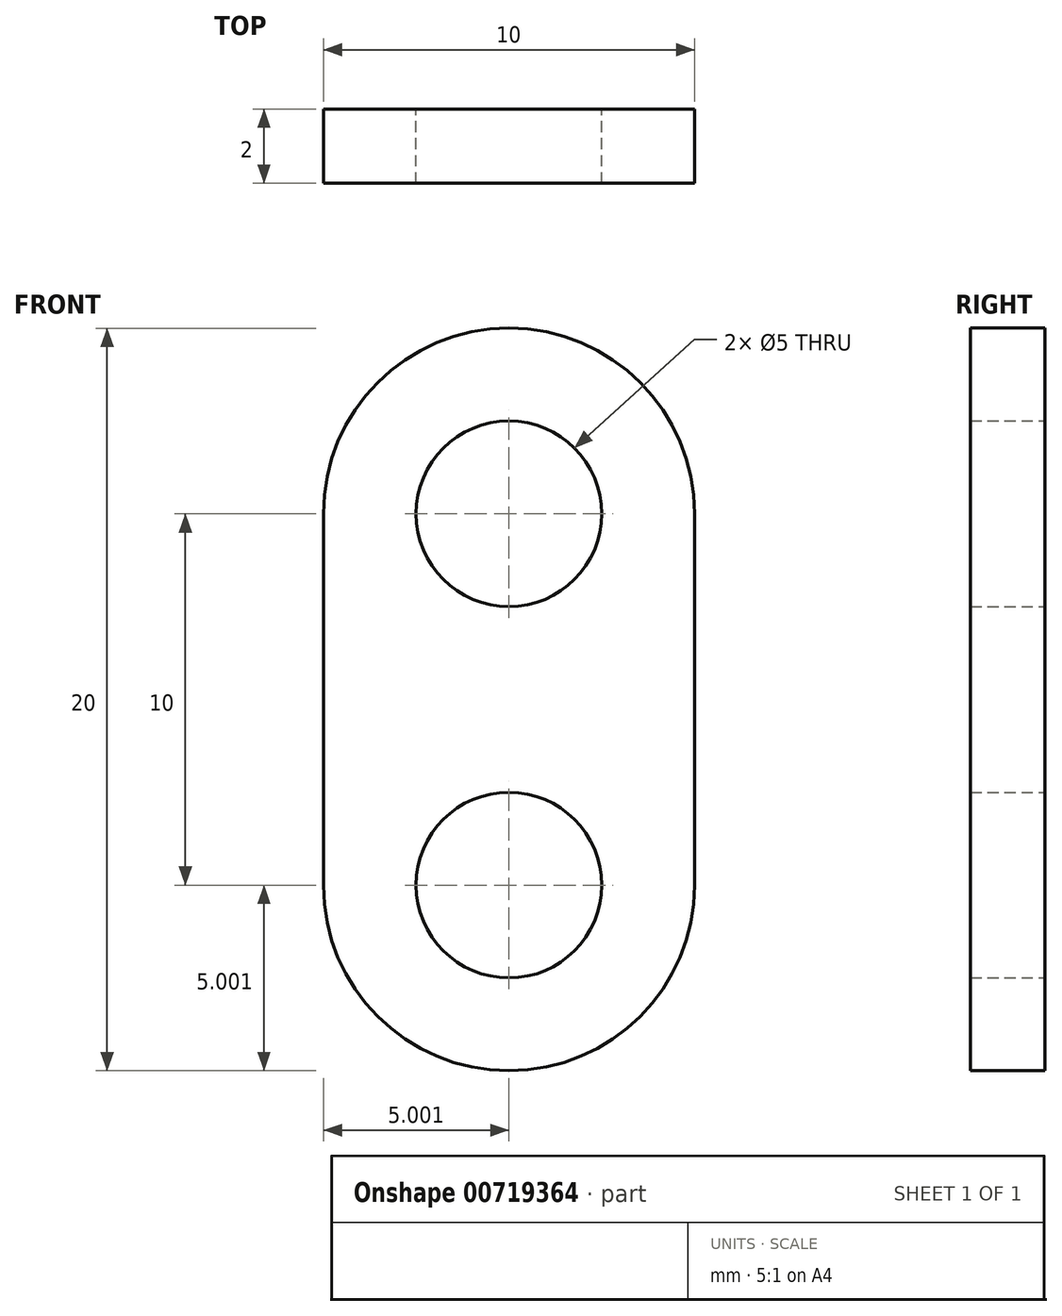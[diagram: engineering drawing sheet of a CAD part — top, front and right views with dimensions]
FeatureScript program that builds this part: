
annotation { "Feature Type Name" : "Feature", "Feature Type Description" : "" }
export const myFeature = defineFeature(function(context is Context, id is Id, definition is map)
    precondition{}
    {
        {
            var Q0;
            Q0=qCreatedBy(makeId("Front.planeOp"),FACE);
            var sketch = newSketch(context, id + "F0", { "sketchPlane" : qUnion([Q0])});
            skLineSegment(sketch, "E0.bottom", {"start": v(27.47, 35.97) * mm, "end": v(27.47, 35.97) * mm});
            skLineSegment(sketch, "E0.top", {"start": v(27.47, 15.97) * mm, "end": v(27.47, 15.97) * mm});
            skLineSegment(sketch, "E0.left", {"start": v(22.47, 30.97) * mm, "end": v(22.47, 20.97) * mm});
            skLineSegment(sketch, "E0.right", {"start": v(32.47, 30.97) * mm, "end": v(32.47, 20.97) * mm});
            skPoint(sketch, "E1.visualSharp", {"position": v(22.47, 35.97) * mm});
            skArc(sketch, "E1.filletArc", {"start": v(27.47, 35.97) * mm, "mid": v(23.94, 34.5) * mm, "end": v(22.47, 30.97) * mm});
            skPoint(sketch, "E2.visualSharp", {"position": v(32.47, 35.97) * mm});
            skArc(sketch, "E2.filletArc", {"start": v(32.47, 30.97) * mm, "mid": v(31, 34.5) * mm, "end": v(27.47, 35.97) * mm});
            skPoint(sketch, "E3.visualSharp", {"position": v(22.47, 15.97) * mm});
            skArc(sketch, "E3.filletArc", {"start": v(22.47, 20.97) * mm, "mid": v(23.94, 17.44) * mm, "end": v(27.47, 15.97) * mm});
            skPoint(sketch, "E4.visualSharp", {"position": v(32.47, 15.97) * mm});
            skArc(sketch, "E4.filletArc", {"start": v(27.47, 15.97) * mm, "mid": v(31, 17.44) * mm, "end": v(32.47, 20.97) * mm});
            skCircle(sketch, "E5", {"center": v(27.47, 30.97) * mm, "radius": 2.5 * mm});
            skCircle(sketch, "E6", {"center": v(27.47, 20.97) * mm, "radius": 2.5 * mm});
            skSolve(sketch);
        }
        {
            var Q0;
            Q0 = qSketchRegion(id + "F0", true);
            extrude(context, id + "F1", {"entities" : qUnion([Q0]), "depth" : 2 * mm, "offsetDistance" : 25.4 * mm});
        }
    });
